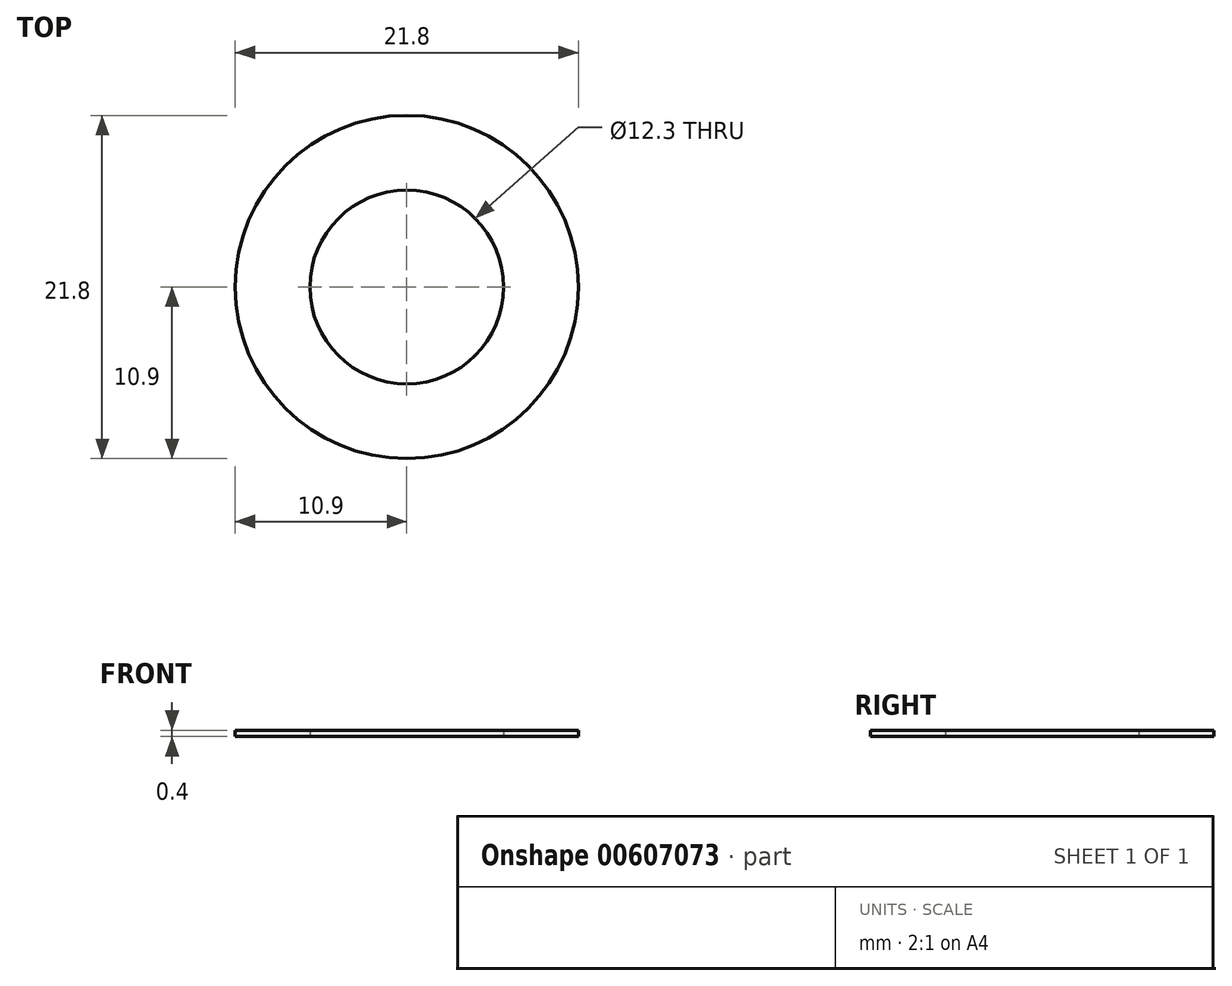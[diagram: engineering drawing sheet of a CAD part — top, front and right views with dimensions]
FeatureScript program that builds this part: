
annotation { "Feature Type Name" : "Feature", "Feature Type Description" : "" }
export const myFeature = defineFeature(function(context is Context, id is Id, definition is map)
    precondition{}
    {
        {
            var Q0;
            Q0=qCreatedBy(makeId("Top.planeOp"),FACE);
            var sketch = newSketch(context, id + "F0", { "sketchPlane" : qUnion([Q0]) });
            skCircle(sketch, "E0", {"center": v(0, 0) * mm, "radius": 10.9 * mm});
            skCircle(sketch, "E1", {"center": v(0, 0) * mm, "radius": 6.15 * mm});
            skSolve(sketch);
        }
        {
            var Q0;
            Q0=makeQuery(id+"F0.imprint","IMPRINT",FACE,{"disambiguationData":[TD([[makeQuery(id+"F0.imprint","IMPRINT",EDGE,{"derivedFrom":sQuery(id+"F0.wireOp",EDGE,"E0")}),1.0]])]});
            extrude(context, id + "F1", {"entities" : qUnion([Q0]), "depth" : 0.4 * mm, "offsetDistance" : 25 * mm});
        }
    });
